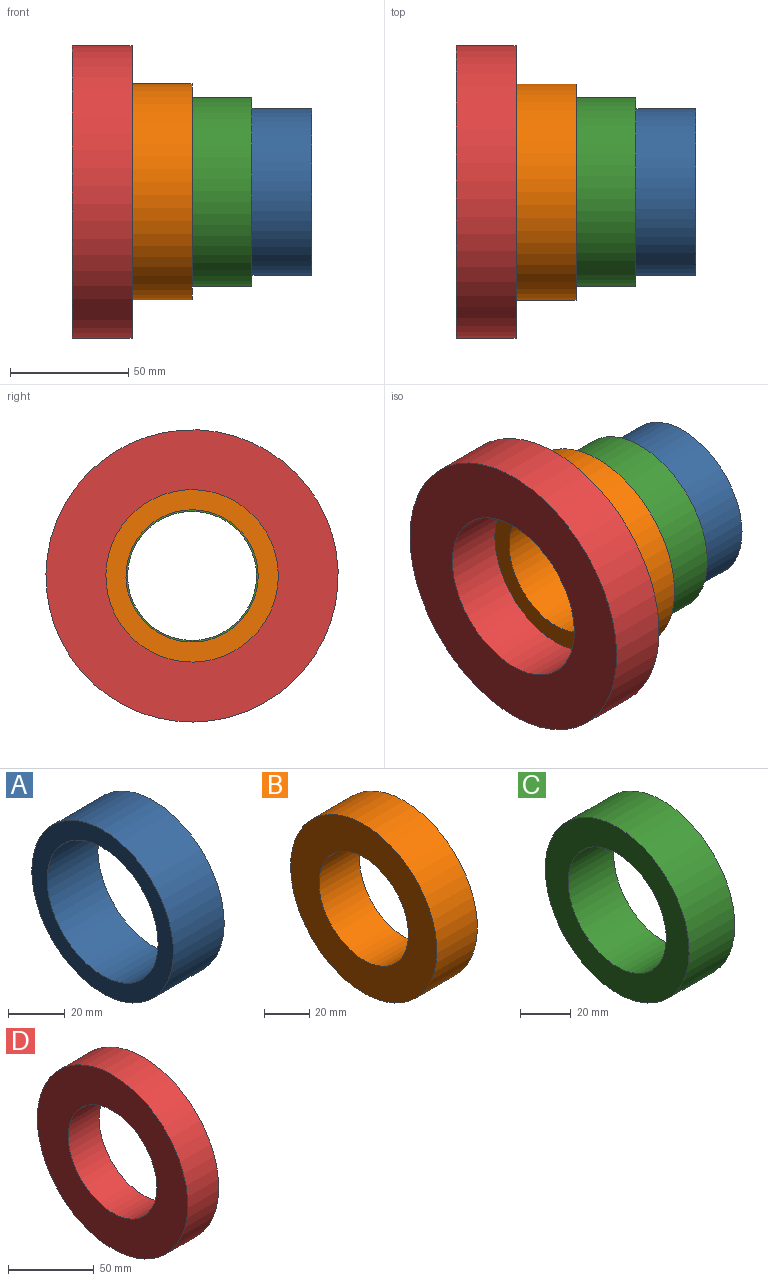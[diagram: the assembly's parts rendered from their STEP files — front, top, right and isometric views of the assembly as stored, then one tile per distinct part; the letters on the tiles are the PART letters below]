
ASSEMBLY  parts=4 mates=3
PART A: 4 faces, bbox 25.4x70.7x70.7 mm
  f0: cylinder r=35.36mm len=70.73mm, axis (-1,0,0), area 5643.6mm2, adj f1,f3
  f1: plane 70.73x70.73mm, normal (-1,0,0), area 1510.7mm2, adj f0,f2
  f2: cylinder r=27.74mm len=55.49mm, axis (-1,0,0), area 4427.5mm2, adj f1,f3
  f3: plane 70.73x70.73mm, normal (1,0,0), area 1510.7mm2, adj f0,f2
PART B: 4 faces, bbox 25.4x91.6x91.6 mm
  f0: cylinder r=45.78mm len=91.56mm, axis (-1,0,0), area 7306.5mm2, adj f1,f3
  f1: plane 91.56x91.56mm, normal (-1,0,0), area 4121.4mm2, adj f0,f2
  f2: cylinder r=28mm len=56mm, axis (-1,0,0), area 4468.9mm2, adj f1,f3
  f3: plane 91.56x91.56mm, normal (1,0,0), area 4121.4mm2, adj f0,f2
PART C: 4 faces, bbox 25.4x80x80 mm
  f0: cylinder r=40.01mm len=80.02mm, axis (-1,0,0), area 6385.6mm2, adj f1,f3
  f1: plane 80.02x80.02mm, normal (-1,0,0), area 2686.1mm2, adj f0,f2
  f2: cylinder r=27.31mm len=54.62mm, axis (-1,0,0), area 4358.8mm2, adj f1,f3
  f3: plane 80.02x80.02mm, normal (1,0,0), area 2686.1mm2, adj f0,f2
PART D: 4 faces, bbox 25.4x123.8x123.8 mm
  f0: cylinder r=61.9mm len=123.8mm, axis (-1,0,0), area 9879.1mm2, adj f1,f3
  f1: plane 123.8x123.8mm, normal (-1,0,0), area 7852.3mm2, adj f0,f2
  f2: cylinder r=36.5mm len=73mm, axis (-1,0,0), area 5825.5mm2, adj f1,f3
  f3: plane 123.8x123.8mm, normal (1,0,0), area 7852.3mm2, adj f0,f2
PLACE A rot(axis=(-1,0,0),44.8deg) t=(-173.58,-28.93,166.58)mm
PLACE B t=(-226.64,-28.93,166.58)mm
PLACE C rot(axis=(-1,0,0),44.8deg) t=(-199.74,-28.93,166.58)mm
PLACE D rot(axis=(0,0.38,-0.92),180deg) t=(-204.74,-28.93,166.58)mm
MATE revolute B.f0 <-> C.f0  axis (1,0,0) through (-191.95,-28.93,166.58)mm
MATE revolute D.f0 <-> B.f0  axis (1,0,0) through (-217.35,-28.93,166.58)mm
MATE revolute C.f0 <-> A.f0  axis (1,0,0) through (-166.55,-28.93,166.58)mm
